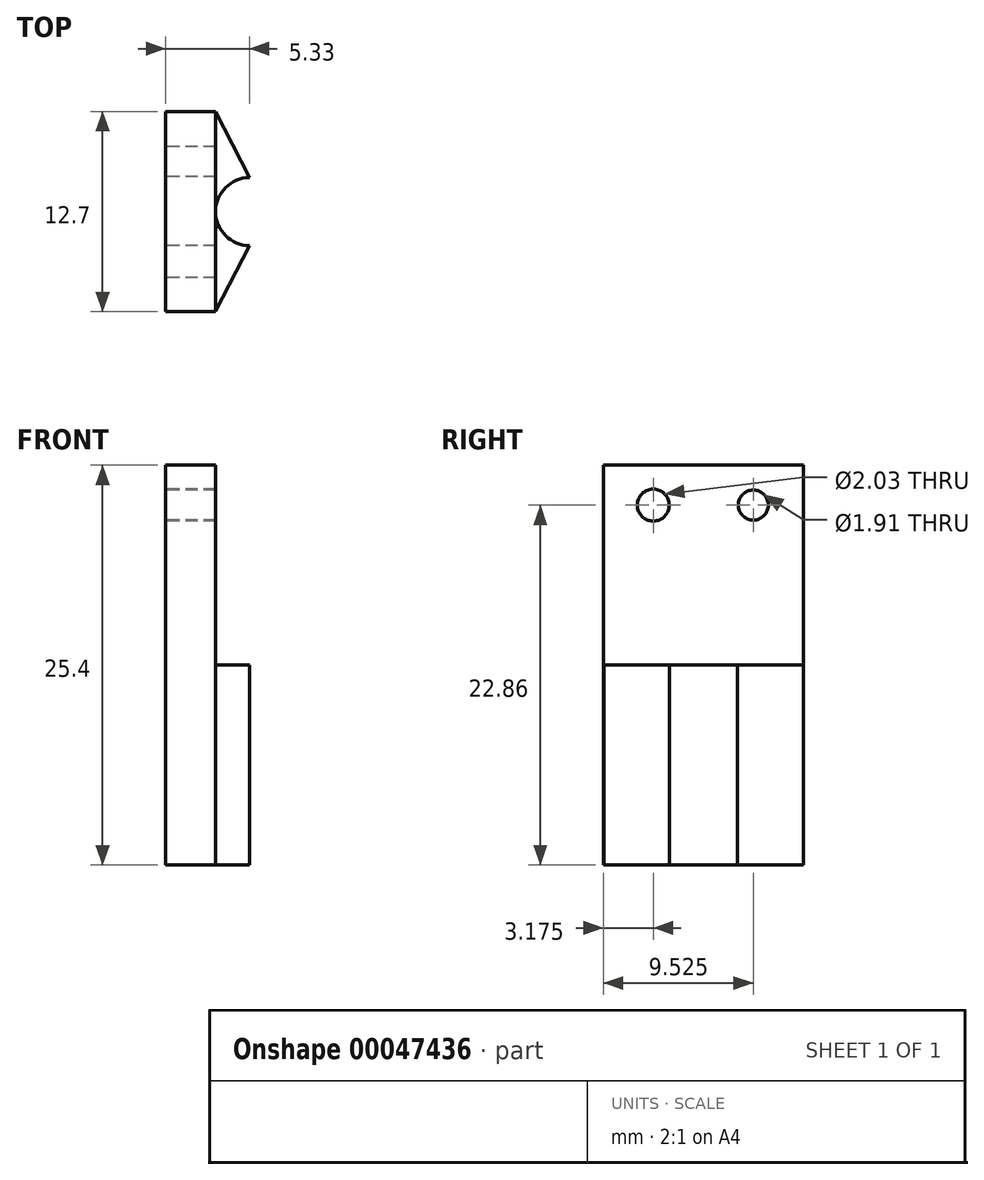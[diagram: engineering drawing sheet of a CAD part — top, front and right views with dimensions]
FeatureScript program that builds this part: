
annotation { "Feature Type Name" : "Feature", "Feature Type Description" : "" }
export const myFeature = defineFeature(function(context is Context, id is Id, definition is map)
    precondition{}
    {
        {
            var Q0;
            Q0=qCreatedBy(makeId("Right.planeOp"),FACE);
            var sketch = newSketch(context, id + "F0", { "sketchPlane" : qUnion([Q0])});
            skLineSegment(sketch, "E0.bottom", {"start": v(0, 0) * mm, "end": v(-12.7, 0) * mm});
            skLineSegment(sketch, "E0.top", {"start": v(0, 25.4) * mm, "end": v(-12.7, 25.4) * mm});
            skLineSegment(sketch, "E0.left", {"start": v(0, 0) * mm, "end": v(0, 25.4) * mm});
            skLineSegment(sketch, "E0.right", {"start": v(-12.7, 0) * mm, "end": v(-12.7, 25.4) * mm});
            skCircle(sketch, "E1", {"center": v(-9.53, 22.86) * mm, "radius": 1.01 * mm});
            skCircle(sketch, "E2", {"center": v(-3.18, 22.86) * mm, "radius": 0.95 * mm});
            skLineSegment(sketch, "E3", {"start": v(-9.53, 22.86) * mm, "end": v(-3.18, 22.86) * mm, "construction": true});
            skPoint(sketch, "E4", {"position": v(-6.35, 25.4) * mm});
            skPoint(sketch, "E5", {"position": v(-6.35, 22.86) * mm});
            skSolve(sketch);
        }
        {
            var Q0;
            Q0=makeQuery(id+"F0.imprint","IMPRINT",FACE,{"disambiguationData":[TD([[makeQuery(id+"F0.imprint","IMPRINT",EDGE,{"derivedFrom":sQuery(id+"F0.wireOp",EDGE,"E0.bottom")}),-1.0]])]});
            extrude(context, id + "F1", {"entities" : qUnion([Q0]), "depth" : 3.17 * mm});
        }
        {
            var Q0;
            Q0=qCreatedBy(makeId("Top.planeOp"),FACE);
            var sketch = newSketch(context, id + "F2", { "sketchPlane" : qUnion([Q0])});
            skArc(sketch, "E6", {"start": v(5.33, -4.2) * mm, "mid": v(3.17, -6.35) * mm, "end": v(5.33, -8.5) * mm});
            skPoint(sketch, "E7", {"position": v(0, -6.35) * mm});
            skLineSegment(sketch, "E8", {"start": v(5.33, -4.2) * mm, "end": v(3.17, 0) * mm});
            skLineSegment(sketch, "E9", {"start": v(5.33, -8.5) * mm, "end": v(3.17, -12.66) * mm});
            skLineSegment(sketch, "E10", {"start": v(3.17, 0) * mm, "end": v(3.17, -12.66) * mm});
            skSolve(sketch);
        }
        {
            var Q0;
            Q0 = qSketchRegion(id + "F2", true);
            extrude(context, id + "F3", {"entities" : qUnion([Q0]), "operationType" : NewBodyOperationType.ADD, "depth" : 12.7 * mm});
        }
    });
